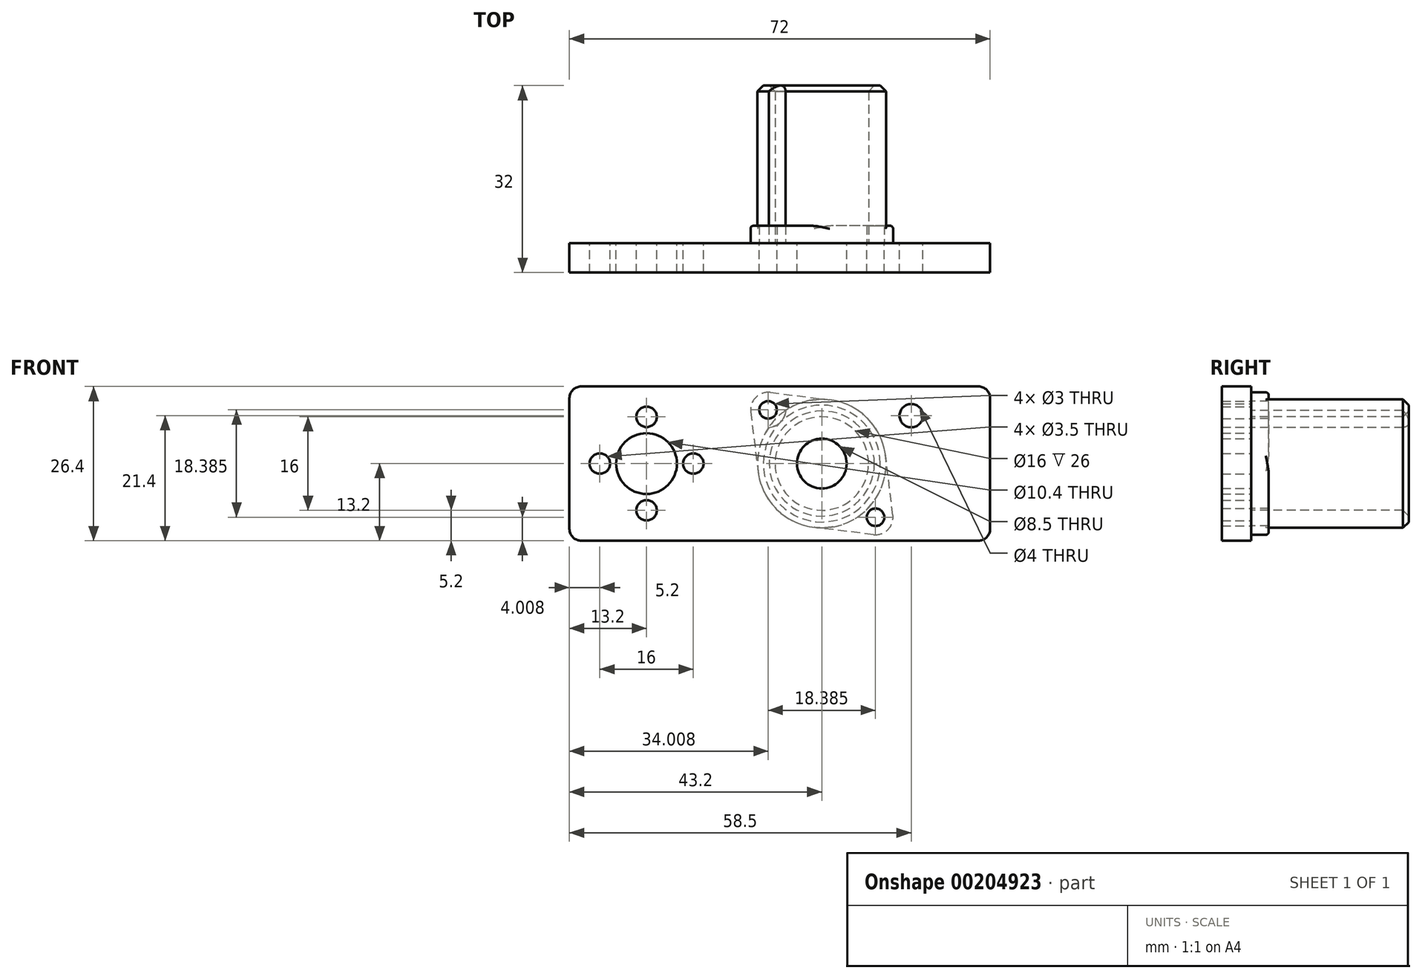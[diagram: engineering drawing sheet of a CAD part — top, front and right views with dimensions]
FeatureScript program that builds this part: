
annotation { "Feature Type Name" : "Feature", "Feature Type Description" : "" }
export const myFeature = defineFeature(function(context is Context, id is Id, definition is map)
    precondition{}
    {
        {
            var Q0;
            Q0=qCreatedBy(makeId("Front.planeOp"),FACE);
            var sketch = newSketch(context, id + "F0", { "sketchPlane" : qUnion([Q0])});
            skLineSegment(sketch, "E0.bottom", {"start": v(0, 0) * mm, "end": v(72, 0) * mm});
            skLineSegment(sketch, "E0.top", {"start": v(0, 26.4) * mm, "end": v(72, 26.4) * mm});
            skLineSegment(sketch, "E0.left", {"start": v(0, 0) * mm, "end": v(0, 26.4) * mm});
            skLineSegment(sketch, "E0.right", {"start": v(72, 0) * mm, "end": v(72, 26.4) * mm});
            skLineSegment(sketch, "E1", {"start": v(0, 13.2) * mm, "end": v(72, 13.2) * mm, "construction": true});
            skCircle(sketch, "E2", {"center": v(13.2, 13.2) * mm, "radius": 5.2 * mm});
            skCircle(sketch, "E3", {"center": v(43.2, 13.2) * mm, "radius": 4.25 * mm});
            skLineSegment(sketch, "E4", {"start": v(56.4, 0) * mm, "end": v(43.2, 13.2) * mm, "construction": true});
            skLineSegment(sketch, "E5", {"start": v(43.2, 13.2) * mm, "end": v(30, 26.4) * mm, "construction": true});
            skCircle(sketch, "E6", {"center": v(34, 22.4) * mm, "radius": 1.5 * mm});
            skCircle(sketch, "E7", {"center": v(52.4, 4) * mm, "radius": 1.5 * mm});
            skLineSegment(sketch, "E8", {"start": v(13.2, 13.2) * mm, "end": v(13.2, 5.2) * mm, "construction": true});
            skCircle(sketch, "E9", {"center": v(13.2, 5.2) * mm, "radius": 1.75 * mm});
            skCircle(sketch, "E10", {"center": v(5.2, 13.2) * mm, "radius": 1.75 * mm});
            skLineSegment(sketch, "E11", {"start": v(13.2, 13.2) * mm, "end": v(13.2, 21.2) * mm});
            skCircle(sketch, "E12", {"center": v(13.2, 21.2) * mm, "radius": 1.75 * mm});
            skCircle(sketch, "E13", {"center": v(21.2, 13.2) * mm, "radius": 1.75 * mm});
            skLineSegment(sketch, "E14", {"start": v(58.5, 13.2) * mm, "end": v(58.5, 26.4) * mm});
            skPoint(sketch, "E15", {"position": v(58.5, 21.4) * mm});
            skCircle(sketch, "E16", {"center": v(58.5, 21.4) * mm, "radius": 2 * mm});
            skSolve(sketch);
        }
        {
            var Q0;
            Q0=makeQuery(id+"F0.imprint","IMPRINT",FACE,{"disambiguationData":[TD([[makeQuery(id+"F0.imprint","IMPRINT",EDGE,{"derivedFrom":sQuery(id+"F0.wireOp",EDGE,"E0.bottom")}),1.0]])]});
            extrude(context, id + "F1", {"entities" : qUnion([Q0]), "depth" : 5 * mm});
        }
        {
            var Q0;
            Q0=makeQuery(id+"F1.opExtrude","SWEPT_EDGE",EDGE,{"disambiguationData":[OSD([sQuery(id+"F0.wireOp",EDGE,"E0.bottom"),sQuery(id+"F0.wireOp",EDGE,"E0.left")])]});
            var Q1;
            Q1=makeQuery(id+"F1.opExtrude","SWEPT_EDGE",EDGE,{"disambiguationData":[OSD([sQuery(id+"F0.wireOp",EDGE,"E0.top"),sQuery(id+"F0.wireOp",EDGE,"E0.left")])]});
            var Q2;
            Q2=makeQuery(id+"F1.opExtrude","SWEPT_EDGE",EDGE,{"disambiguationData":[OSD([sQuery(id+"F0.wireOp",EDGE,"E0.bottom"),sQuery(id+"F0.wireOp",EDGE,"E0.right")])]});
            var Q3;
            Q3=makeQuery(id+"F1.opExtrude","SWEPT_EDGE",EDGE,{"disambiguationData":[OSD([sQuery(id+"F0.wireOp",EDGE,"E0.top"),sQuery(id+"F0.wireOp",EDGE,"E0.right")])]});
            fillet(context, id + "F2", {"entities" : qUnion([Q0, Q1, Q2, Q3]), "radius" : 2 * mm, "tangentPropagation" : true, "allowEdgeOverflow" : false});
        }
        {
            var Q0;
            Q0=makeQuery(id+"F1.opExtrude","CAP_FACE",FACE,{"disambiguationData":[OSD([sQuery(id+"F0.wireOp",EDGE,"E0.bottom"),sQuery(id+"F0.wireOp",EDGE,"E0.top"),sQuery(id+"F0.wireOp",EDGE,"E0.left"),sQuery(id+"F0.wireOp",EDGE,"E0.right"),sQuery(id+"F0.wireOp",EDGE,"E2"),sQuery(id+"F0.wireOp",EDGE,"E3"),sQuery(id+"F0.wireOp",EDGE,"E6"),sQuery(id+"F0.wireOp",EDGE,"E7"),sQuery(id+"F0.wireOp",EDGE,"E9"),sQuery(id+"F0.wireOp",EDGE,"E10"),sQuery(id+"F0.wireOp",EDGE,"E12"),sQuery(id+"F0.wireOp",EDGE,"E13")])],"isStart":true});
            var sketch = newSketch(context, id + "F3", { "sketchPlane" : qUnion([Q0])});
            skCircle(sketch, "E17", {"center": v(-43.2, 13.2) * mm, "radius": 8 * mm});
            skCircle(sketch, "E18", {"center": v(-43.2, 13.2) * mm, "radius": 11 * mm});
            skCircle(sketch, "E19", {"center": v(-52.4, 4) * mm, "radius": 3 * mm});
            skCircle(sketch, "E20", {"center": v(-52.4, 4) * mm, "radius": 1.5 * mm});
            skLineSegment(sketch, "E21", {"start": v(-55.37, 4.37) * mm, "end": v(-54.12, 14.54) * mm});
            skLineSegment(sketch, "E22", {"start": v(-52.03, 1.03) * mm, "end": v(-41.86, 2.28) * mm});
            skCircle(sketch, "E23", {"center": v(-34, 22.4) * mm, "radius": 3 * mm});
            skCircle(sketch, "E24", {"center": v(-34, 22.4) * mm, "radius": 1.5 * mm});
            skLineSegment(sketch, "E25", {"start": v(-31.03, 22.03) * mm, "end": v(-32.28, 11.86) * mm});
            skLineSegment(sketch, "E26", {"start": v(-34.37, 25.37) * mm, "end": v(-44.54, 24.12) * mm});
            skSolve(sketch);
        }
        {
            var Q0;
            {var subQ0=sQuery(id+"F3.wireOp",EDGE,"E21");Q0=makeQuery(id+"F3.imprint","IMPRINT",FACE,{"disambiguationData":[TD([[makeQuery(id+"F3.imprint","IMPRINT",EDGE,{"derivedFrom":subQ0}),-1.0]])]});}
            var Q1;
            Q1=makeQuery(id+"F3.imprint","IMPRINT",FACE,{"disambiguationData":[TD([[makeQuery(id+"F3.imprint","IMPRINT",EDGE,{"derivedFrom":sQuery(id+"F3.wireOp",EDGE,"E20")}),1.0]])]});
            var Q2;
            {var subQ0=sQuery(id+"F3.wireOp",EDGE,"E19");var subQ1=sQuery(id+"F3.wireOp",EDGE,"E18");var subQ2=makeQuery(id+"F3.imprint","INTERSECT",VERTEX,{"disambiguationData":[OD(0.0)],"derivedFrom":[subQ1,subQ0]});Q2=makeQuery(id+"F3.imprint","IMPRINT",FACE,{"disambiguationData":[TD([[makeQuery(id+"F3.imprint","IMPRINT",EDGE,{"disambiguationData":[TD([[subQ2,-1.0]])],"derivedFrom":subQ1}),1.0]])]});}
            var Q3;
            {var subQ0=sQuery(id+"F3.wireOp",EDGE,"E22");Q3=makeQuery(id+"F3.imprint","IMPRINT",FACE,{"disambiguationData":[TD([[makeQuery(id+"F3.imprint","IMPRINT",EDGE,{"derivedFrom":subQ0}),1.0]])]});}
            var Q4;
            Q4=makeQuery(id+"F3.imprint","IMPRINT",FACE,{"disambiguationData":[TD([[makeQuery(id+"F3.imprint","IMPRINT",EDGE,{"derivedFrom":sQuery(id+"F3.wireOp",EDGE,"E17")}),-1.0]])]});
            var Q5;
            {var subQ0=sQuery(id+"F3.wireOp",EDGE,"E23");var subQ1=sQuery(id+"F3.wireOp",EDGE,"E18");var subQ2=makeQuery(id+"F3.imprint","INTERSECT",VERTEX,{"disambiguationData":[OD(0.0)],"derivedFrom":[subQ1,subQ0]});Q5=makeQuery(id+"F3.imprint","IMPRINT",FACE,{"disambiguationData":[TD([[makeQuery(id+"F3.imprint","IMPRINT",EDGE,{"disambiguationData":[TD([[subQ2,1.0]])],"derivedFrom":subQ1}),1.0]])]});}
            var Q6;
            Q6=makeQuery(id+"F3.imprint","IMPRINT",FACE,{"disambiguationData":[TD([[makeQuery(id+"F3.imprint","IMPRINT",EDGE,{"derivedFrom":sQuery(id+"F3.wireOp",EDGE,"E24")}),1.0]])]});
            var Q7;
            {var subQ0=sQuery(id+"F3.wireOp",EDGE,"E25");Q7=makeQuery(id+"F3.imprint","IMPRINT",FACE,{"disambiguationData":[TD([[makeQuery(id+"F3.imprint","IMPRINT",EDGE,{"derivedFrom":subQ0}),-1.0]])]});}
            var Q8;
            {var subQ0=sQuery(id+"F3.wireOp",EDGE,"E26");Q8=makeQuery(id+"F3.imprint","IMPRINT",FACE,{"disambiguationData":[TD([[makeQuery(id+"F3.imprint","IMPRINT",EDGE,{"derivedFrom":subQ0}),1.0]])]});}
            extrude(context, id + "F4", {"entities" : qUnion([Q0, Q1, Q2, Q3, Q4, Q5, Q6, Q7, Q8]), "depth" : 3 * mm});
        }
        {
            var Q0;
            Q0=makeQuery(id+"F4.opExtrude","CAP_FACE",FACE,{"disambiguationData":[OSD([sQuery(id+"F3.wireOp",EDGE,"E17"),sQuery(id+"F3.wireOp",EDGE,"E18"),sQuery(id+"F3.wireOp",EDGE,"E19"),sQuery(id+"F3.wireOp",EDGE,"E20"),sQuery(id+"F3.wireOp",EDGE,"E21"),sQuery(id+"F3.wireOp",EDGE,"E22"),sQuery(id+"F3.wireOp",EDGE,"E23"),sQuery(id+"F3.wireOp",EDGE,"E24"),sQuery(id+"F3.wireOp",EDGE,"E25"),sQuery(id+"F3.wireOp",EDGE,"E26")])],"isStart":false});
            var sketch = newSketch(context, id + "F5", { "sketchPlane" : qUnion([Q0])});
            skCircle(sketch, "E27", {"center": v(-43.2, 13.2) * mm, "radius": 8 * mm});
            skCircle(sketch, "E28", {"center": v(-43.2, 13.2) * mm, "radius": 11 * mm});
            skSolve(sketch);
        }
        {
            var Q0;
            Q0=makeQuery(id+"F5.imprint","IMPRINT",FACE,{"disambiguationData":[TD([[makeQuery(id+"F5.imprint","IMPRINT",EDGE,{"derivedFrom":sQuery(id+"F5.wireOp",EDGE,"E27")}),-1.0]])]});
            extrude(context, id + "F6", {"entities" : qUnion([Q0]), "operationType" : NewBodyOperationType.ADD, "depth" : 24 * mm});
        }
        {
            var Q0;
            Q0=makeQuery(id+"F6.opExtrude","CAP_EDGE",EDGE,{"disambiguationData":[OSD([sQuery(id+"F5.wireOp",EDGE,"E27")])],"isStart":false});
            var Q1;
            Q1=makeQuery(id+"F6.opExtrude","CAP_EDGE",EDGE,{"disambiguationData":[OSD([sQuery(id+"F5.wireOp",EDGE,"E28")])],"isStart":false});
            chamfer(context, id + "F7", {"entities" : qUnion([Q0, Q1]), "width" : 1 * mm, "tangentPropagation" : true});
        }
        {
            var Q0;
            Q0=makeQuery(id+"F4.opExtrude","CAP_EDGE",EDGE,{"disambiguationData":[OSD([sQuery(id+"F3.wireOp",EDGE,"E22")])],"isStart":false});
            var Q1;
            Q1=makeQuery(id+"F4.opExtrude","CAP_EDGE",EDGE,{"disambiguationData":[OSD([sQuery(id+"F3.wireOp",EDGE,"E19")])],"isStart":false});
            var Q2;
            Q2=makeQuery(id+"F4.opExtrude","CAP_EDGE",EDGE,{"disambiguationData":[OSD([sQuery(id+"F3.wireOp",EDGE,"E21")])],"isStart":false});
            var Q3;
            Q3=makeQuery(id+"F4.opExtrude","CAP_EDGE",EDGE,{"disambiguationData":[OSD([sQuery(id+"F3.wireOp",EDGE,"E25")])],"isStart":false});
            fillet(context, id + "F8", {"entities" : qUnion([Q0, Q1, Q2, Q3]), "radius" : .5 * mm, "tangentPropagation" : true, "allowEdgeOverflow" : false});
        }
    });
